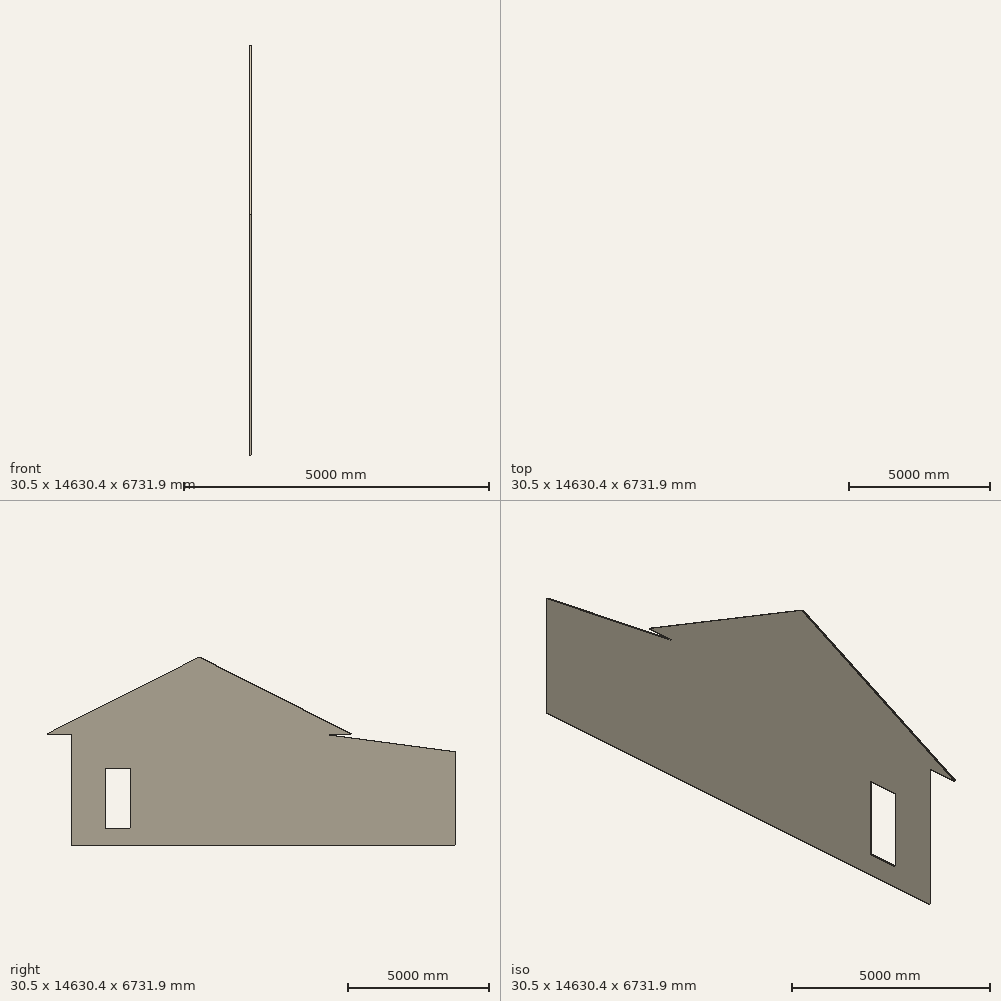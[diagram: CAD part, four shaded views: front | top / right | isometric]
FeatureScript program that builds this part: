
annotation { "Feature Type Name" : "Feature", "Feature Type Description" : "" }
export const myFeature = defineFeature(function(context is Context, id is Id, definition is map)
    precondition{}
    {
        {
            var Q0;
            Q0=qCreatedBy(makeId("Right.planeOp"),FACE);
            var sketch = newSketch(context, id + "F0", { "sketchPlane" : qUnion([Q0])});
            skLineSegment(sketch, "E0", {"start": v(0, 0) * mm, "end": v(-4572, 0) * mm});
            skLineSegment(sketch, "E1", {"start": v(0, 0) * mm, "end": v(4572, 0) * mm});
            skLineSegment(sketch, "E2", {"start": v(0, 0) * mm, "end": v(0, 2286) * mm});
            skLineSegment(sketch, "E3", {"start": v(-4572, 0) * mm, "end": v(0, 2286) * mm});
            skLineSegment(sketch, "E4", {"start": v(10.2, 2312.34) * mm, "end": v(4572, 0) * mm});
            skLineSegment(sketch, "E5", {"start": v(-4572, 0) * mm, "end": v(-5486.4, 0) * mm});
            skLineSegment(sketch, "E6", {"start": v(10.2, 2312.34) * mm, "end": v(10.2, 2769.54) * mm});
            skLineSegment(sketch, "E7", {"start": v(-5486.4, 0) * mm, "end": v(10.2, 2769.54) * mm});
            skLineSegment(sketch, "E8", {"start": v(4572, 0) * mm, "end": v(5486.4, 0) * mm});
            skLineSegment(sketch, "E9", {"start": v(10.2, 2769.54) * mm, "end": v(5486.4, 0) * mm});
            skLineSegment(sketch, "E10", {"start": v(-4572, 0) * mm, "end": v(-4572, -3352.8) * mm});
            skLineSegment(sketch, "E11", {"start": v(4572, 0) * mm, "end": v(4572, -3352.8) * mm});
            skLineSegment(sketch, "E12", {"start": v(4572, -3352.8) * mm, "end": v(-4572, -3352.8) * mm});
            skLineSegment(sketch, "E13", {"start": v(-4572, -3352.8) * mm, "end": v(-4572, -3962.4) * mm});
            skLineSegment(sketch, "E14", {"start": v(4572, -3352.8) * mm, "end": v(4572, -3962.4) * mm});
            skLineSegment(sketch, "E15", {"start": v(4572, -3962.4) * mm, "end": v(-4572, -3962.4) * mm});
            skLineSegment(sketch, "E16", {"start": v(4572, -3962.4) * mm, "end": v(9144, -3962.4) * mm});
            skLineSegment(sketch, "E17", {"start": v(4572, -3352.8) * mm, "end": v(9144, -3352.8) * mm});
            skLineSegment(sketch, "E18", {"start": v(9144, -3352.8) * mm, "end": v(9144, -3962.4) * mm});
            skLineSegment(sketch, "E19", {"start": v(9144, -3352.8) * mm, "end": v(9144, -609.6) * mm});
            skLineSegment(sketch, "E20", {"start": v(4572, 0) * mm, "end": v(9144, -609.6) * mm});
            skLineSegment(sketch, "E21", {"start": v(9144, -609.6) * mm, "end": v(9144, -1219.2) * mm});
            skLineSegment(sketch, "E22", {"start": v(9144, -1219.2) * mm, "end": v(4572, -609.6) * mm});
            skLineSegment(sketch, "E23", {"start": v(-3352.8, -3352.8) * mm, "end": v(-3352.8, -1219.2) * mm});
            skLineSegment(sketch, "E24", {"start": v(-3352.8, -1219.2) * mm, "end": v(-2438.4, -1219.2) * mm});
            skLineSegment(sketch, "E25", {"start": v(-2438.4, -1219.2) * mm, "end": v(-2438.4, -3352.8) * mm});
            skLineSegment(sketch, "E26.0", {"start": v(-3347.8, -3352.8) * mm, "end": v(-3347.8, -1219.2) * mm});
            skLineSegment(sketch, "E27.0", {"start": v(-2743.2, -1524) * mm, "end": v(-2743.2, -3352.8) * mm});
            skLineSegment(sketch, "E27.1", {"start": v(-3048, -1524) * mm, "end": v(-2743.2, -1524) * mm});
            skLineSegment(sketch, "E27.2", {"start": v(-3048, -3352.8) * mm, "end": v(-3048, -1524) * mm});
            skLineSegment(sketch, "E28", {"start": v(3349.88, -715.82) * mm, "end": v(3349.88, -1700.04) * mm});
            skSolve(sketch);
        }
        {
            var Q0;
            Q0 = qSketchRegion(id + "F0", true);
            extrude(context, id + "F1", {"entities" : qUnion([Q0]), "depth" : 30.48 * mm, "offsetDistance" : 30.48 * mm});
        }
    });
